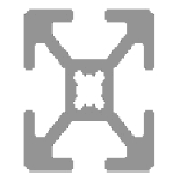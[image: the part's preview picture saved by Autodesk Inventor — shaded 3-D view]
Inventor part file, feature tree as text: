
AUTODESK INVENTOR PART (.ipt)
format: ipt  version: 2013 SP2 (Build 170200200, 200)  size: 235,520 bytes
history: native  units: in
note: dims shown in document units (in); Inventor stores cm internally (conversion verified against a paired STEP export)
features: other x5, sketch x3, plane x1
ambient origin geometry x8: Origin, YZ Plane, XZ Plane, XY Plane, X Axis, Y Axis, Z Axis, Center Point
bodies: Solid1 (feature_tree), Body (feature_tree)
feature tree (9):
  other  "Driven Length"
  other  "Frame Generator"
  other  "Blocks"
  other  "Start Plane"
  other  "End Plane"
  sketch  "Sketch"  dims[d4=0.13in d5=0.0in d6=90.0deg d7=1.9685in]
  sketch  "Sketch2"  dims[d2=0.7874in]
  plane  "Work Plane3"
  sketch  "Sketch3"  dims[d3=2.7559in]
